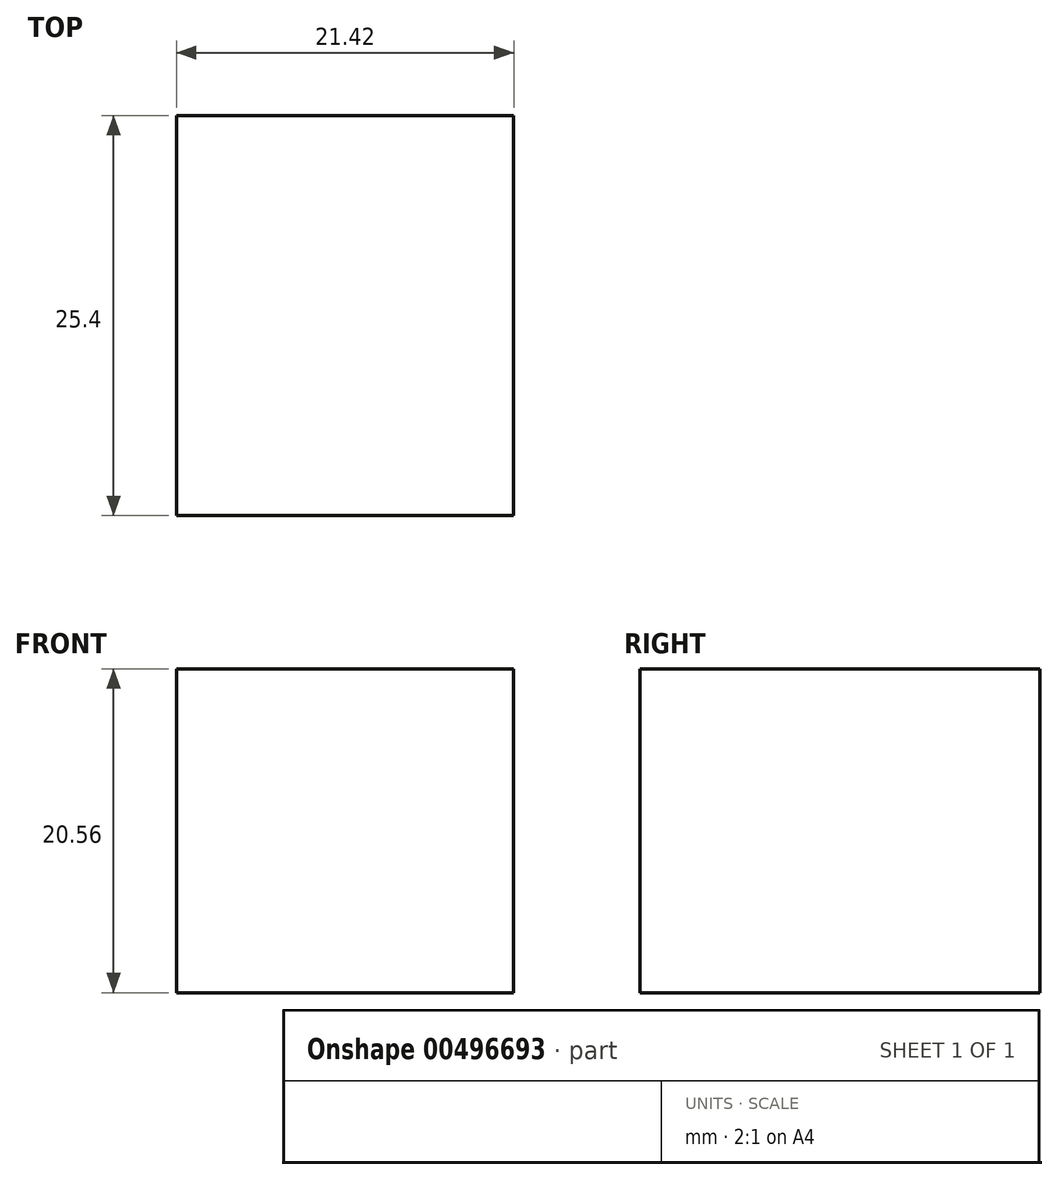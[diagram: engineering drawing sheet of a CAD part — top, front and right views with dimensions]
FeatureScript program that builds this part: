
annotation { "Feature Type Name" : "Feature", "Feature Type Description" : "" }
export const myFeature = defineFeature(function(context is Context, id is Id, definition is map)
    precondition{}
    {
        {
            var Q0;
            Q0=qCreatedBy(makeId("Front.planeOp"),FACE);
            var sketch = newSketch(context, id + "F0", { "sketchPlane" : qUnion([Q0])});
            skLineSegment(sketch, "E0.bottom", {"start": v(0, 0) * mm, "end": v(21.42, 0) * mm});
            skLineSegment(sketch, "E0.top", {"start": v(0, -20.56) * mm, "end": v(21.42, -20.56) * mm});
            skLineSegment(sketch, "E0.left", {"start": v(0, 0) * mm, "end": v(0, -20.56) * mm});
            skLineSegment(sketch, "E0.right", {"start": v(21.42, 0) * mm, "end": v(21.42, -20.56) * mm});
            skSolve(sketch);
        }
        {
            var Q0;
            Q0=makeQuery(id+"F0.imprint","IMPRINT",FACE,{"disambiguationData":[TD([[makeQuery(id+"F0.imprint","IMPRINT",EDGE,{"derivedFrom":sQuery(id+"F0.wireOp",EDGE,"E0.bottom")}),-1.0]])]});
            extrude(context, id + "F1", {"entities" : qUnion([Q0]), "endBound" : BoundingType.SYMMETRIC, "depth" : 25.4 * mm});
        }
    });
